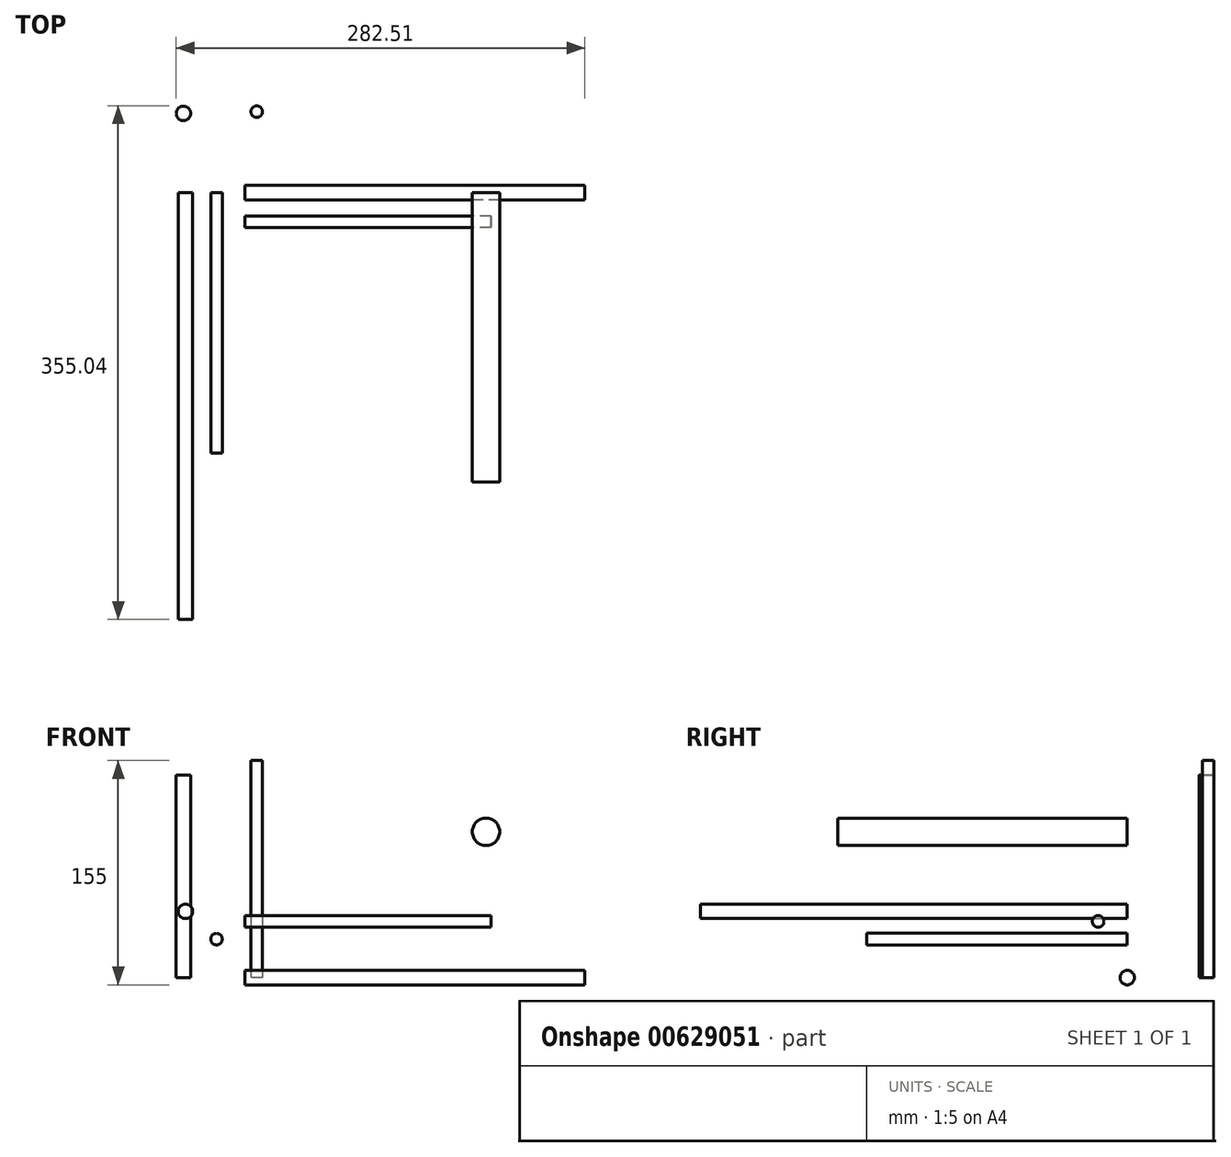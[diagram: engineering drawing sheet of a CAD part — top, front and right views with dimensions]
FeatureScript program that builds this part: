
annotation { "Feature Type Name" : "Feature", "Feature Type Description" : "" }
export const myFeature = defineFeature(function(context is Context, id is Id, definition is map)
    precondition{}
    {
        {
            var Q0;
            Q0=qCreatedBy(makeId("Right.planeOp"),FACE);
            var sketch = newSketch(context, id + "F0", { "sketchPlane" : qUnion([Q0])});
            skCircle(sketch, "E0", {"center": v(0, 0) * mm, "radius": 5 * mm});
            skCircle(sketch, "E1", {"center": v(-20.14, 38.84) * mm, "radius": 4 * mm});
            skSolve(sketch);
        }
        {
            var Q0;
            Q0=makeQuery(id+"F0.imprint","IMPRINT",FACE,{"disambiguationData":[TD([[makeQuery(id+"F0.imprint","IMPRINT",EDGE,{"derivedFrom":sQuery(id+"F0.wireOp",EDGE,"E0")}),1.0]])]});
            extrude(context, id + "F1", {"entities" : qUnion([Q0]), "depth" : 235 * mm, "offsetDistance" : 25 * mm});
        }
        {
            var Q0;
            Q0=qCreatedBy(makeId("Front.planeOp"),FACE);
            var sketch = newSketch(context, id + "F2", { "sketchPlane" : qUnion([Q0])});
            skCircle(sketch, "E2", {"center": v(-41.13, 45.79) * mm, "radius": 5 * mm});
            skCircle(sketch, "E3", {"center": v(-19.67, 26.6) * mm, "radius": 4 * mm});
            skSolve(sketch);
        }
        {
            var Q0;
            Q0=makeQuery(id+"F2.imprint","IMPRINT",FACE,{"disambiguationData":[TD([[makeQuery(id+"F2.imprint","IMPRINT",EDGE,{"derivedFrom":sQuery(id+"F2.wireOp",EDGE,"E2")}),1.0]])]});
            extrude(context, id + "F3", {"entities" : qUnion([Q0]), "depth" : 295 * mm, "offsetDistance" : 25 * mm});
        }
        {
            var Q0;
            Q0=qCreatedBy(makeId("Top.planeOp"),FACE);
            var sketch = newSketch(context, id + "F4", { "sketchPlane" : qUnion([Q0])});
            skCircle(sketch, "E4", {"center": v(-42.5, 54.83) * mm, "radius": 5 * mm});
            skCircle(sketch, "E5", {"center": v(8.1, 56.04) * mm, "radius": 4 * mm});
            skSolve(sketch);
        }
        {
            var Q0;
            Q0=makeQuery(id+"F4.imprint","IMPRINT",FACE,{"disambiguationData":[TD([[makeQuery(id+"F4.imprint","IMPRINT",EDGE,{"derivedFrom":sQuery(id+"F4.wireOp",EDGE,"E4")}),1.0]])]});
            extrude(context, id + "F5", {"entities" : qUnion([Q0]), "depth" : 140 * mm, "offsetDistance" : 25 * mm});
        }
        {
            var Q0;
            Q0=makeQuery(id+"F1.opExtrude","SWEPT_BODY",BODY,{"disambiguationData":[OSD([sQuery(id+"F0.wireOp",EDGE,"E0")])]});
            transform(context, id + "F6", {"entities" : qUnion([Q0]), "transformType" : TransformType.TRANSLATION_3D, "dx" : 0 * mm, "dy" : 0 * mm, "dz" : 0 * mm, "makeCopy" : true});
        }
        {
            var Q0;
            Q0=qCreatedBy(makeId("Front.planeOp"),FACE);
            var sketch = newSketch(context, id + "F7", { "sketchPlane" : qUnion([Q0])});
            skCircle(sketch, "E6", {"center": v(166.66, 100.77) * mm, "radius": 9.47 * mm});
            skSolve(sketch);
        }
        {
            var Q0;
            Q0=makeQuery(id+"F7.imprint","IMPRINT",FACE,{"disambiguationData":[TD([[makeQuery(id+"F7.imprint","IMPRINT",EDGE,{"derivedFrom":sQuery(id+"F7.wireOp",EDGE,"E6")}),1.0]])]});
            extrude(context, id + "F8", {"entities" : qUnion([Q0]), "depth" : 200 * mm, "offsetDistance" : 25 * mm});
        }
        {
            var Q0;
            Q0=makeQuery(id+"F6.opPattern","COPY",BODY,{"derivedFrom":makeQuery(id+"F1.opExtrude","SWEPT_BODY",BODY,{"disambiguationData":[OSD([sQuery(id+"F0.wireOp",EDGE,"E0")])]}),"instanceName":"1"});
            deleteBodies(context, id + "F9", {"entities" : qUnion([Q0])});
        }
        {
            var Q0;
            Q0=makeQuery(id+"F0.imprint","IMPRINT",FACE,{"disambiguationData":[TD([[makeQuery(id+"F0.imprint","IMPRINT",EDGE,{"derivedFrom":sQuery(id+"F0.wireOp",EDGE,"E1")}),1.0]])]});
            extrude(context, id + "F10", {"entities" : qUnion([Q0]), "operationType" : NewBodyOperationType.ADD, "depth" : 170 * mm, "offsetDistance" : 25 * mm});
        }
        {
            var Q0;
            Q0=makeQuery(id+"F2.imprint","IMPRINT",FACE,{"disambiguationData":[TD([[makeQuery(id+"F2.imprint","IMPRINT",EDGE,{"derivedFrom":sQuery(id+"F2.wireOp",EDGE,"E3")}),1.0]])]});
            extrude(context, id + "F11", {"entities" : qUnion([Q0]), "depth" : 180 * mm, "offsetDistance" : 25 * mm});
        }
        {
            var Q0;
            Q0=makeQuery(id+"F4.imprint","IMPRINT",FACE,{"disambiguationData":[TD([[makeQuery(id+"F4.imprint","IMPRINT",EDGE,{"derivedFrom":sQuery(id+"F4.wireOp",EDGE,"E5")}),1.0]])]});
            extrude(context, id + "F12", {"entities" : qUnion([Q0]), "depth" : 150 * mm, "offsetDistance" : 25 * mm});
        }
    });
